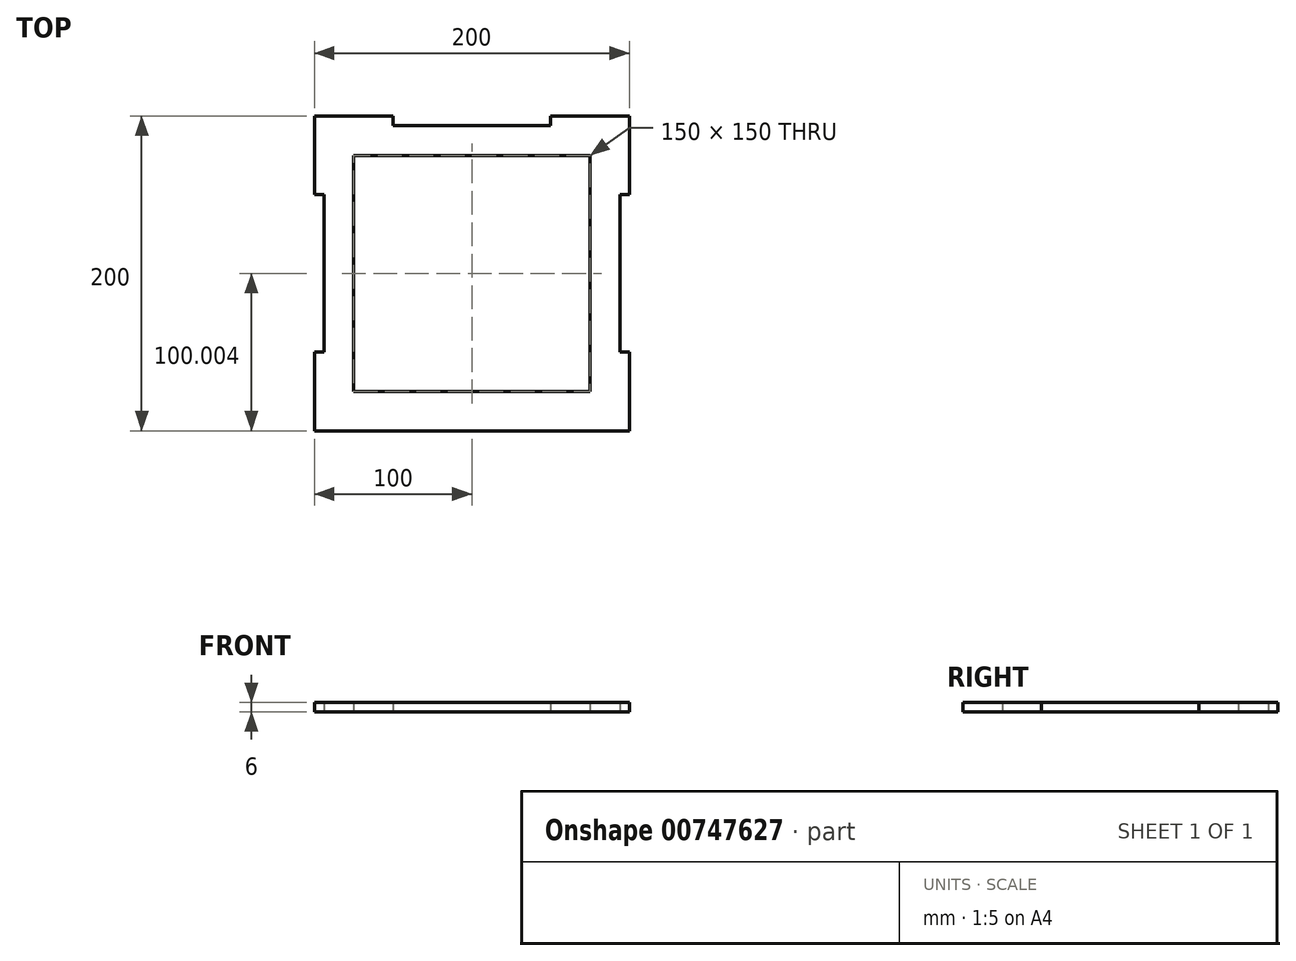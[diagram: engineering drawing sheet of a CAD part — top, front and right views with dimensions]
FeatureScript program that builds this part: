
annotation { "Feature Type Name" : "Feature", "Feature Type Description" : "" }
export const myFeature = defineFeature(function(context is Context, id is Id, definition is map)
    precondition{}
    {
        {
            var Q0;
            Q0=qCreatedBy(makeId("Top.planeOp"),FACE);
            var sketch = newSketch(context, id + "F0", { "sketchPlane" : qUnion([Q0])});
            skLineSegment(sketch, "E0.bottom", {"start": v(-100, 119.82) * mm, "end": v(-50, 119.82) * mm});
            skLineSegment(sketch, "E0.top", {"start": v(-100, -80.18) * mm, "end": v(100, -80.18) * mm});
            skLineSegment(sketch, "E0.left", {"start": v(-100, 119.82) * mm, "end": v(-100, 69.82) * mm});
            skLineSegment(sketch, "E0.right", {"start": v(100, 119.82) * mm, "end": v(100, 69.82) * mm});
            skLineSegment(sketch, "E1.bottom", {"start": v(-100, 69.82) * mm, "end": v(-94, 69.82) * mm});
            skLineSegment(sketch, "E1.top", {"start": v(-100, -30.18) * mm, "end": v(-94, -30.18) * mm});
            skLineSegment(sketch, "E1.right", {"start": v(-94, 69.82) * mm, "end": v(-94, -30.18) * mm});
            skLineSegment(sketch, "E2.bottom", {"start": v(100, 69.82) * mm, "end": v(94, 69.82) * mm});
            skLineSegment(sketch, "E2.top", {"start": v(100, -30.18) * mm, "end": v(94, -30.18) * mm});
            skLineSegment(sketch, "E2.right", {"start": v(94, 69.82) * mm, "end": v(94, -30.18) * mm});
            skLineSegment(sketch, "E3.trimOffspring", {"start": v(-100, -30.18) * mm, "end": v(-100, -80.18) * mm});
            skLineSegment(sketch, "E4.trimOffspring", {"start": v(100, -30.18) * mm, "end": v(100, -80.18) * mm});
            skLineSegment(sketch, "E5.top", {"start": v(-50, 113.82) * mm, "end": v(50, 113.82) * mm});
            skLineSegment(sketch, "E5.left", {"start": v(-50, 119.82) * mm, "end": v(-50, 113.82) * mm});
            skLineSegment(sketch, "E5.right", {"start": v(50, 119.82) * mm, "end": v(50, 113.82) * mm});
            skLineSegment(sketch, "E6.trimOffspring", {"start": v(50, 119.82) * mm, "end": v(100, 119.82) * mm});
            skLineSegment(sketch, "E7.bottom", {"start": v(-75, 94.82) * mm, "end": v(75, 94.82) * mm});
            skLineSegment(sketch, "E7.top", {"start": v(-75, -55.18) * mm, "end": v(75, -55.18) * mm});
            skLineSegment(sketch, "E7.left", {"start": v(-75, 94.82) * mm, "end": v(-75, -55.18) * mm});
            skLineSegment(sketch, "E7.right", {"start": v(75, 94.82) * mm, "end": v(75, -55.18) * mm});
            skLineSegment(sketch, "E8", {"start": v(-75, 36.52) * mm, "end": v(-94, 36.52) * mm, "construction": true});
            skPoint(sketch, "E8.endSnap0", {"position": v(-94, 19.82) * mm});
            skLineSegment(sketch, "E9", {"start": v(75, 50.14) * mm, "end": v(94, 50.14) * mm, "construction": true});
            skLineSegment(sketch, "E10", {"start": v(33.87, -55.18) * mm, "end": v(33.87, -80.18) * mm, "construction": true});
            skLineSegment(sketch, "E11", {"start": v(61.12, 119.82) * mm, "end": v(61.12, 94.82) * mm, "construction": true});
            skSolve(sketch);
        }
        {
            var Q0;
            Q0=makeQuery(id+"F0.imprint","IMPRINT",FACE,{"disambiguationData":[TD([[makeQuery(id+"F0.imprint","IMPRINT",EDGE,{"derivedFrom":sQuery(id+"F0.wireOp",EDGE,"E0.bottom")}),-1.0]])]});
            extrude(context, id + "F1", {"entities" : qUnion([Q0]), "depth" : 6 * mm, "offsetDistance" : 25.4 * mm});
        }
    });
